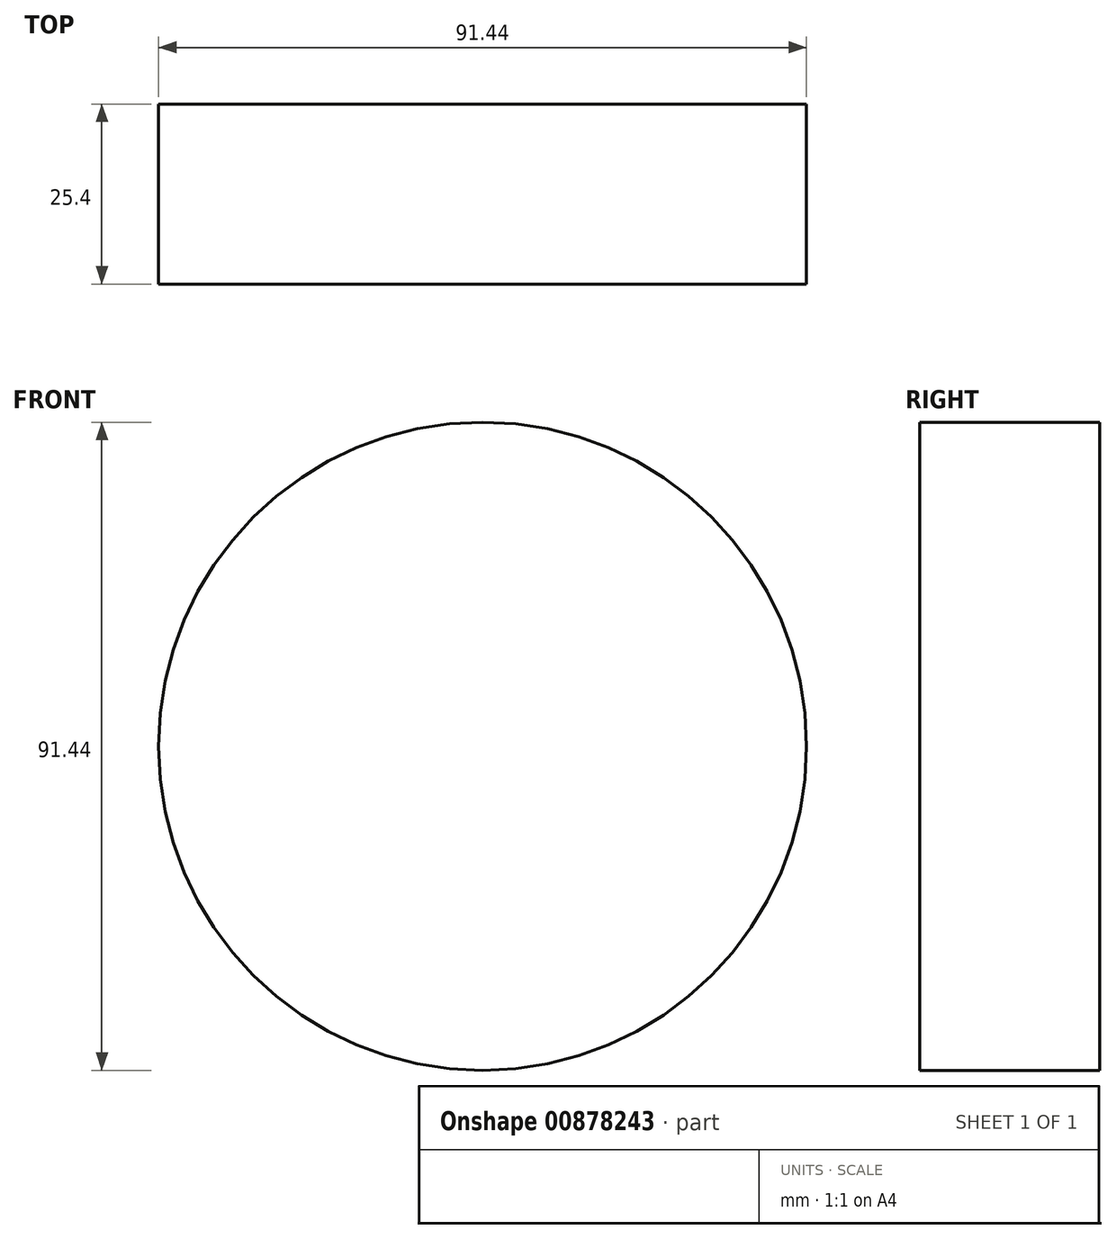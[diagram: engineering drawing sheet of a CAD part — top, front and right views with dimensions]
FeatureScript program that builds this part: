
annotation { "Feature Type Name" : "Feature", "Feature Type Description" : "" }
export const myFeature = defineFeature(function(context is Context, id is Id, definition is map)
    precondition{}
    {
        {
            var Q0;
            Q0=qCreatedBy(makeId("Front.planeOp"),FACE);
            var sketch = newSketch(context, id + "F0", { "sketchPlane" : qUnion([Q0])});
            skCircle(sketch, "E0", {"center": v(0, 0) * mm, "radius": 45.72 * mm});
            skSolve(sketch);
        }
        {
            var Q0;
            Q0 = qBodyType(qCreatedBy(id + "F0" ,EDGE), BodyType.WIRE);
            var Q1;
            Q1=sQuery(id+"F0.wireOp",EDGE,"E0");
            extrude(context, id + "F1", {"bodyType" : ToolBodyType.SURFACE, "surfaceEntities" : qUnion([Q0, Q1]), "depth" : 25.4 * mm, "offsetDistance" : 25.4 * mm});
        }
    });
